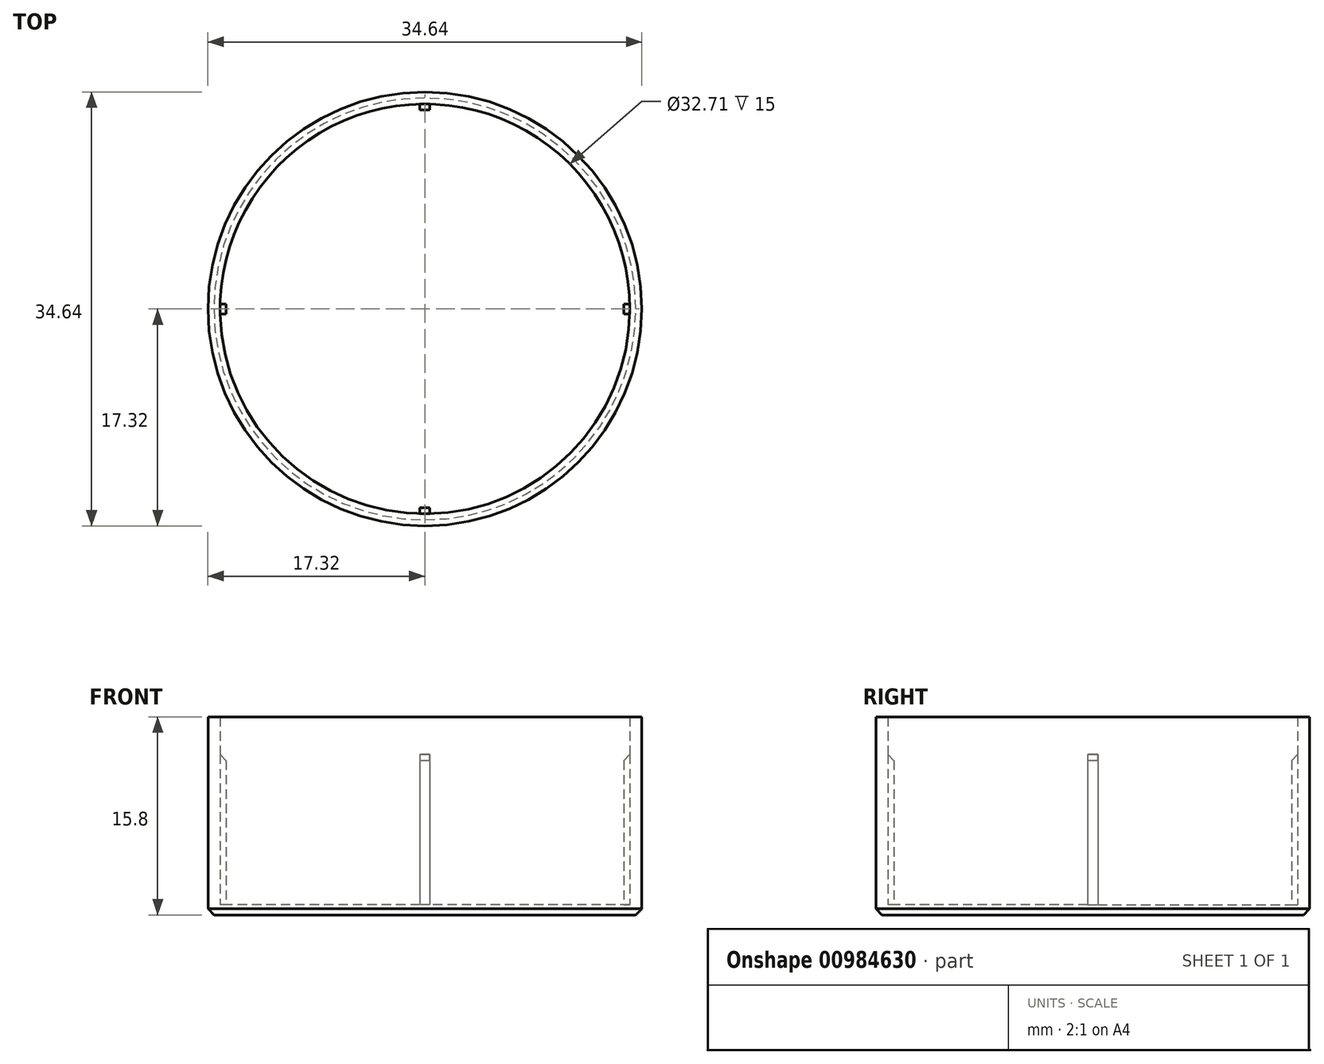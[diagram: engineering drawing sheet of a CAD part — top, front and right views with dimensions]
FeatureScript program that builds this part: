
annotation { "Feature Type Name" : "Feature", "Feature Type Description" : "" }
export const myFeature = defineFeature(function(context is Context, id is Id, definition is map)
    precondition{}
    {
        {
            assignVariable(context, id + "F0", {"name" : "height", "anyValue" : 15});
        }
        {
            var Q0;
            Q0=qCreatedBy(makeId("Top.planeOp"),FACE);
            var sketch = newSketch(context, id + "F1", { "sketchPlane" : qUnion([Q0])});
            skCircle(sketch, "E0", {"center": v(0, 0) * mm, "radius": 15.88 * mm, "construction": true});
            skCircle(sketch, "E1.0", {"center": v(0, 0) * mm, "radius": 16.36 * mm});
            skCircle(sketch, "E2.0", {"center": v(0, 0) * mm, "radius": 17.32 * mm});
            skLineSegment(sketch, "E3.bottom", {"start": v(-0.4, 0.4) * mm, "end": v(0.4, 0.4) * mm, "construction": true});
            skLineSegment(sketch, "E3.top", {"start": v(-0.4, -0.4) * mm, "end": v(0.4, -0.4) * mm, "construction": true});
            skLineSegment(sketch, "E3.left", {"start": v(-0.4, 0.4) * mm, "end": v(-0.4, -0.4) * mm, "construction": true});
            skLineSegment(sketch, "E3.right", {"start": v(0.4, 0.4) * mm, "end": v(0.4, -0.4) * mm, "construction": true});
            skPoint(sketch, "E4", {"position": v(0, 0.4) * mm});
            skPoint(sketch, "E5", {"position": v(0.4, 0) * mm});
            skLineSegment(sketch, "E6", {"start": v(-15.87, 0.4) * mm, "end": v(-16.35, 0.4) * mm});
            skLineSegment(sketch, "E7", {"start": v(-15.87, -0.4) * mm, "end": v(-16.35, -0.4) * mm});
            skLineSegment(sketch, "E8", {"start": v(-15.87, 0.4) * mm, "end": v(-15.87, -0.4) * mm});
            skLineSegment(sketch, "E9", {"start": v(15.87, 0.4) * mm, "end": v(16.35, 0.4) * mm});
            skLineSegment(sketch, "E10", {"start": v(15.87, -0.4) * mm, "end": v(16.35, -0.4) * mm});
            skLineSegment(sketch, "E11", {"start": v(15.87, -0.4) * mm, "end": v(15.87, 0.4) * mm});
            skLineSegment(sketch, "E12", {"start": v(-0.4, 16.35) * mm, "end": v(-0.4, 15.87) * mm});
            skLineSegment(sketch, "E13", {"start": v(0.4, 15.87) * mm, "end": v(0.4, 16.35) * mm});
            skLineSegment(sketch, "E14", {"start": v(0.4, 15.87) * mm, "end": v(-0.4, 15.87) * mm});
            skLineSegment(sketch, "E15", {"start": v(0.4, -15.87) * mm, "end": v(0.4, -16.35) * mm});
            skLineSegment(sketch, "E16", {"start": v(-0.4, -15.87) * mm, "end": v(-0.4, -16.35) * mm});
            skLineSegment(sketch, "E17", {"start": v(-0.4, -15.87) * mm, "end": v(0.4, -15.87) * mm});
            skSolve(sketch);
        }
        {
            var Q0;
            Q0 = qSketchRegion(id + "F1", true);
            var Q1;
            {var subQ2=sQuery(id+"F1.wireOp",EDGE,"E6");Q1=makeQuery(id+"F1.imprint","IMPRINT",FACE,{"disambiguationData":[TD([[makeQuery(id+"F1.imprint","IMPRINT",EDGE,{"derivedFrom":subQ2}),-1.0]])]});}
            var Q2;
            {var subQ0=sQuery(id+"F1.wireOp",EDGE,"E6");Q2=makeQuery(id+"F1.imprint","IMPRINT",FACE,{"disambiguationData":[TD([[makeQuery(id+"F1.imprint","IMPRINT",EDGE,{"derivedFrom":subQ0}),1.0]])]});}
            var Q3;
            {var subQ0=sQuery(id+"F1.wireOp",EDGE,"E15");Q3=makeQuery(id+"F1.imprint","IMPRINT",FACE,{"disambiguationData":[TD([[makeQuery(id+"F1.imprint","IMPRINT",EDGE,{"derivedFrom":subQ0}),-1.0]])]});}
            var Q4;
            {var subQ0=sQuery(id+"F1.wireOp",EDGE,"E9");Q4=makeQuery(id+"F1.imprint","IMPRINT",FACE,{"disambiguationData":[TD([[makeQuery(id+"F1.imprint","IMPRINT",EDGE,{"derivedFrom":subQ0}),-1.0]])]});}
            var Q5;
            {var subQ0=sQuery(id+"F1.wireOp",EDGE,"E12");Q5=makeQuery(id+"F1.imprint","IMPRINT",FACE,{"disambiguationData":[TD([[makeQuery(id+"F1.imprint","IMPRINT",EDGE,{"derivedFrom":subQ0}),1.0]])]});}
            extrude(context, id + "F2", {"entities" : qUnion([Q0, Q1, Q2, Q3, Q4, Q5]), "oppositeDirection" : true, "depth" : .8 * mm, "offsetDistance" : 25 * mm});
        }
        {
            var Q0;
            Q0=makeQuery(id+"F1.imprint","IMPRINT",FACE,{"disambiguationData":[TD([[makeQuery(id+"F1.imprint","IMPRINT",EDGE,{"derivedFrom":sQuery(id+"F1.wireOp",EDGE,"E2.0")}),1.0]])]});
            extrude(context, id + "F3", {"entities" : qUnion([Q0]), "operationType" : NewBodyOperationType.ADD, "depth" : (getVariable(context, 'height')) * mm, "offsetDistance" : 25 * mm});
        }
        {
            var Q0;
            {var subQ0=sQuery(id+"F1.wireOp",EDGE,"E12");Q0=makeQuery(id+"F1.imprint","IMPRINT",FACE,{"disambiguationData":[TD([[makeQuery(id+"F1.imprint","IMPRINT",EDGE,{"derivedFrom":subQ0}),1.0]])]});}
            var Q1;
            {var subQ0=sQuery(id+"F1.wireOp",EDGE,"E6");Q1=makeQuery(id+"F1.imprint","IMPRINT",FACE,{"disambiguationData":[TD([[makeQuery(id+"F1.imprint","IMPRINT",EDGE,{"derivedFrom":subQ0}),1.0]])]});}
            var Q2;
            {var subQ0=sQuery(id+"F1.wireOp",EDGE,"E9");Q2=makeQuery(id+"F1.imprint","IMPRINT",FACE,{"disambiguationData":[TD([[makeQuery(id+"F1.imprint","IMPRINT",EDGE,{"derivedFrom":subQ0}),-1.0]])]});}
            var Q3;
            {var subQ0=sQuery(id+"F1.wireOp",EDGE,"E15");Q3=makeQuery(id+"F1.imprint","IMPRINT",FACE,{"disambiguationData":[TD([[makeQuery(id+"F1.imprint","IMPRINT",EDGE,{"derivedFrom":subQ0}),-1.0]])]});}
            extrude(context, id + "F4", {"entities" : qUnion([Q0, Q1, Q2, Q3]), "operationType" : NewBodyOperationType.ADD, "depth" : (getVariable(context, 'height') - 3) * mm, "offsetDistance" : 25 * mm});
        }
        {
            var Q0;
            Q0=makeQuery(id+"F2.opExtrude","CAP_EDGE",EDGE,{"disambiguationData":[OSD([sQuery(id+"F1.wireOp",EDGE,"E2.0")])],"isStart":false});
            chamfer(context, id + "F5", {"entities" : qUnion([Q0]), "width" : .48 * mm, "tangentPropagation" : true});
        }
        {
            var Q0;
            Q0=makeQuery(id+"F4.opExtrude","CAP_EDGE",EDGE,{"disambiguationData":[OSD([sQuery(id+"F1.wireOp",EDGE,"E8")])],"isStart":false});
            var Q1;
            Q1=makeQuery(id+"F4.opExtrude","CAP_EDGE",EDGE,{"disambiguationData":[OSD([sQuery(id+"F1.wireOp",EDGE,"E14")])],"isStart":false});
            var Q2;
            Q2=makeQuery(id+"F4.opExtrude","CAP_EDGE",EDGE,{"disambiguationData":[OSD([sQuery(id+"F1.wireOp",EDGE,"E11")])],"isStart":false});
            var Q3;
            Q3=makeQuery(id+"F4.opExtrude","CAP_EDGE",EDGE,{"disambiguationData":[OSD([sQuery(id+"F1.wireOp",EDGE,"E17")])],"isStart":false});
            chamfer(context, id + "F6", {"entities" : qUnion([Q0, Q1, Q2, Q3]), "width" : .48 * mm, "tangentPropagation" : true});
        }
    });
